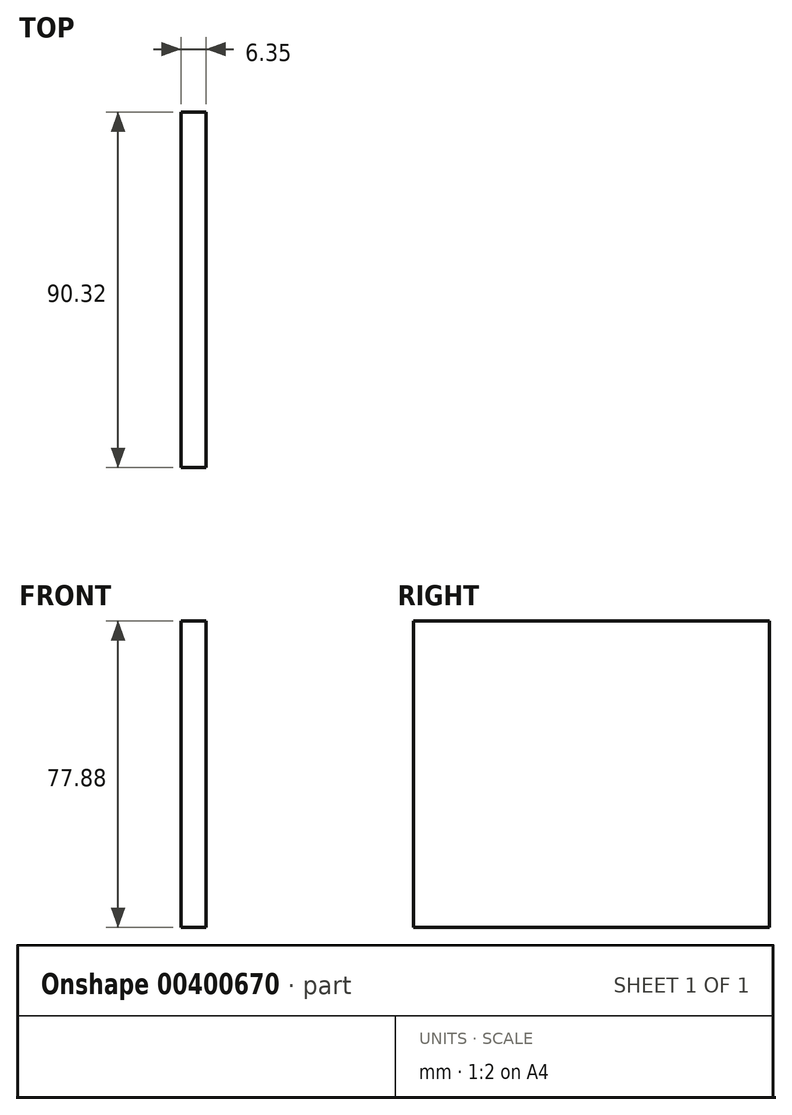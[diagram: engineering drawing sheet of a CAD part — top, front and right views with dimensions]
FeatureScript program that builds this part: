
annotation { "Feature Type Name" : "Feature", "Feature Type Description" : "" }
export const myFeature = defineFeature(function(context is Context, id is Id, definition is map)
    precondition{}
    {
        {
            var Q0;
            Q0=qCreatedBy(makeId("Right.planeOp"),FACE);
            var sketch = newSketch(context, id + "F0", { "sketchPlane" : qUnion([Q0])});
            skLineSegment(sketch, "E0.bottom", {"start": v(-45.16, 38.94) * mm, "end": v(45.16, 38.94) * mm});
            skLineSegment(sketch, "E0.top", {"start": v(-45.16, -38.94) * mm, "end": v(45.16, -38.94) * mm});
            skLineSegment(sketch, "E0.left", {"start": v(-45.16, 38.94) * mm, "end": v(-45.16, -38.94) * mm});
            skLineSegment(sketch, "E0.right", {"start": v(45.16, 38.94) * mm, "end": v(45.16, -38.94) * mm});
            skPoint(sketch, "E0.middle", {"position": v(0, 0) * mm});
            skSolve(sketch);
        }
        {
            var Q0;
            Q0=makeQuery(id+"F0.imprint","IMPRINT",FACE,{"disambiguationData":[TD([[makeQuery(id+"F0.imprint","IMPRINT",EDGE,{"derivedFrom":sQuery(id+"F0.wireOp",EDGE,"E0.bottom")}),-1.0]])]});
            extrude(context, id + "F1", {"entities" : qUnion([Q0]), "depth" : 6.35 * mm});
        }
    });
